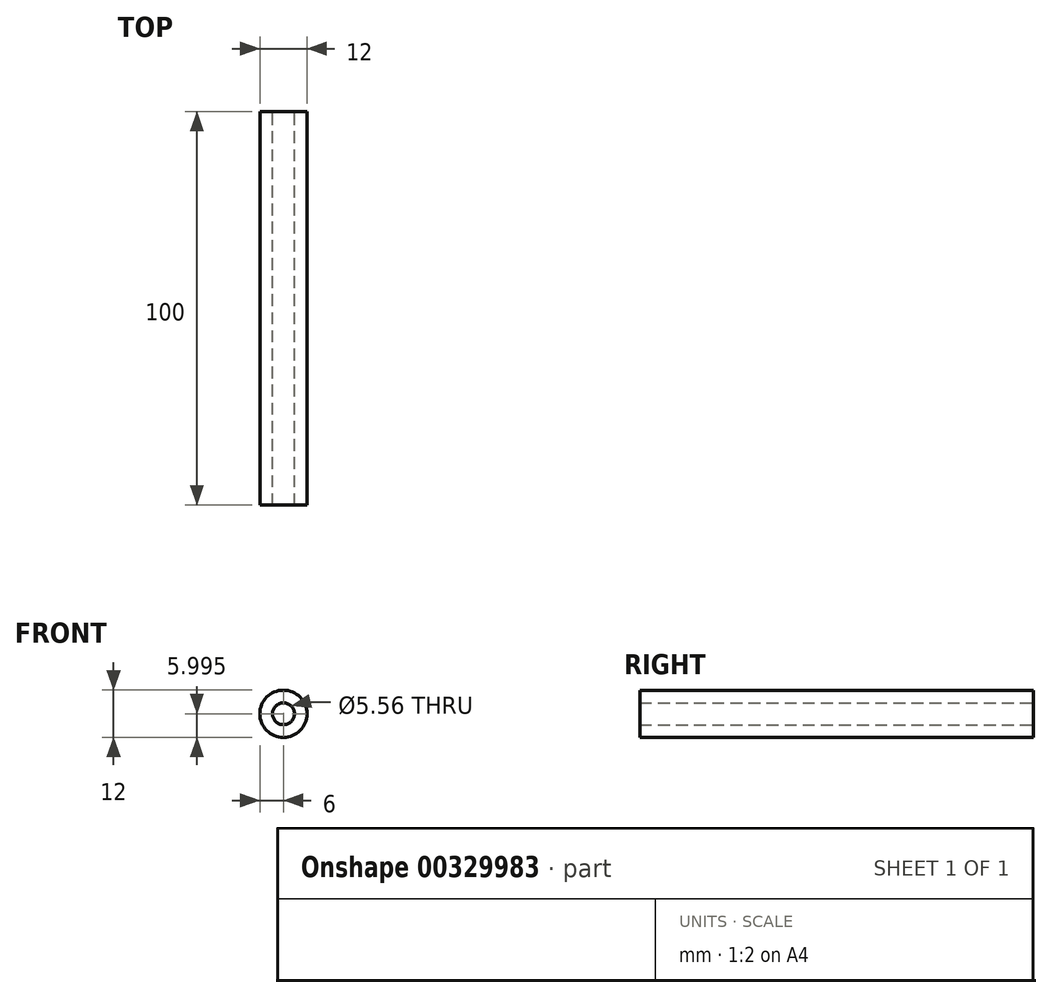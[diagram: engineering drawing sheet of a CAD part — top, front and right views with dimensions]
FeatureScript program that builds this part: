
annotation { "Feature Type Name" : "Feature", "Feature Type Description" : "" }
export const myFeature = defineFeature(function(context is Context, id is Id, definition is map)
    precondition{}
    {
        {
            var Q0;
            Q0=qCreatedBy(makeId("Front.planeOp"),FACE);
            var sketch = newSketch(context, id + "F0", { "sketchPlane" : qUnion([Q0])});
            skCircle(sketch, "E0", {"center": v(0, 10.26) * mm, "radius": 2.78 * mm});
            skCircle(sketch, "E1", {"center": v(0, 10.26) * mm, "radius": 6 * mm});
            skSolve(sketch);
        }
        {
            var Q0;
            Q0=makeQuery(id+"F0.imprint","IMPRINT",FACE,{"disambiguationData":[TD([[makeQuery(id+"F0.imprint","IMPRINT",EDGE,{"derivedFrom":sQuery(id+"F0.wireOp",EDGE,"E0")}),-1.0]])]});
            extrude(context, id + "F1", {"entities" : qUnion([Q0]), "endBound" : BoundingType.SYMMETRIC, "depth" : 100 * mm});
        }
    });
